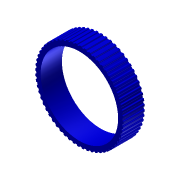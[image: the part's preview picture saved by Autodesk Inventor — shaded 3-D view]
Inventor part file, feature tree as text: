
AUTODESK INVENTOR PART (.ipt)
format: ipt  version: 2011 (Build 150239000, 239)  size: 472,064 bytes
history: native  units: in
note: dims shown in document units (in); Inventor stores cm internally (conversion verified against a paired STEP export)
features: extrude x2, sketch x2, pattern_circular x1
ambient origin geometry x8: Origin, YZ Plane, XZ Plane, XY Plane, X Axis, Y Axis, Z Axis, Center Point
bodies: Solid1 (feature_tree)
feature tree (5):
  extrude  "Extrusion1"  Depth=4.05in
  extrude  "Extrusion2"  Depth=0.0206in
  pattern_circular  "Circular Pattern1"  [2 undecoded]
  sketch  "Sketch1"  dims[d0=3.64in d1=4.05in]
  sketch  "Sketch2"  dims[d2=1.0in d3=0.0in d4=0.0206in d7=0.05in d8=0.025in d10=0.0206in d11=0.025in d12=0.025in d13=1.0in d14=0.0in d15=23.622in d16=360.0deg]
note: 2 required parameter values undecoded (feature->parameter linkage not recoverable at this tier; creation-order binding heuristic only, values carry confidence <= 0.55)
